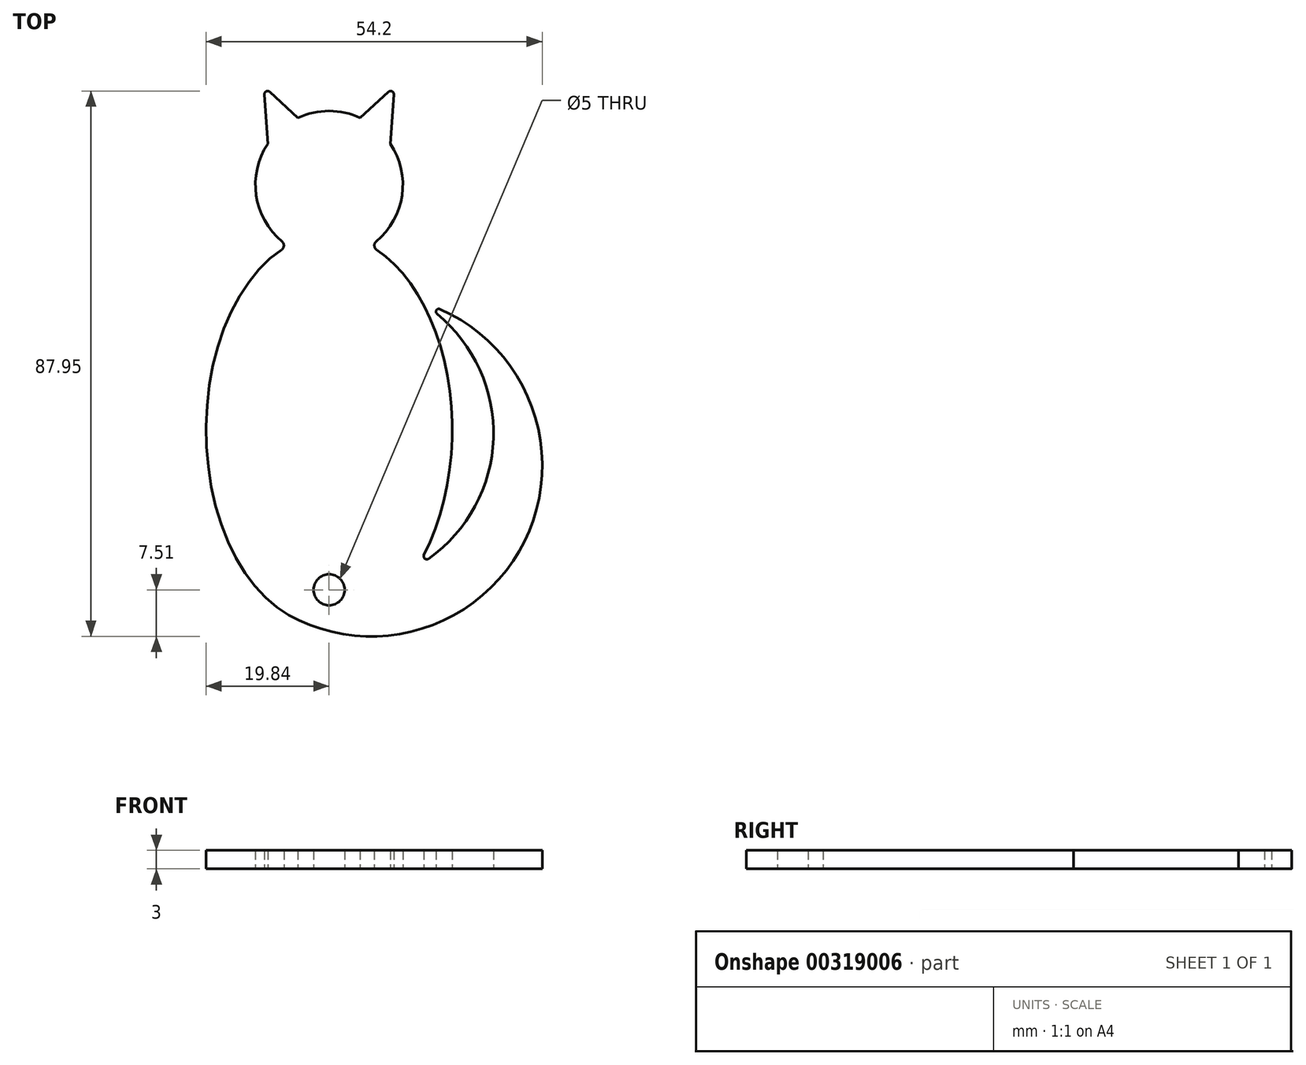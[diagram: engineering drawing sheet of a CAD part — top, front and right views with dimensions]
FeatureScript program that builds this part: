
annotation { "Feature Type Name" : "Feature", "Feature Type Description" : "" }
export const myFeature = defineFeature(function(context is Context, id is Id, definition is map)
    precondition{}
    {
        {
            var Q0;
            Q0=qCreatedBy(makeId("Top.planeOp"),FACE);
            var sketch = newSketch(context, id + "F0", { "sketchPlane" : qUnion([Q0])});
            skEllipticalArc(sketch, "E0", {});
            skArc(sketch, "E1", {"start": v(7.6, 30.45) * mm, "mid": v(11.76, 37.87) * mm, "end": v(9.9, 46.18) * mm});
            skArc(sketch, "E2.trimOffspring", {"start": v(5.02, 50.37) * mm, "mid": v(0, 51.48) * mm, "end": v(-5.02, 50.37) * mm});
            skArc(sketch, "E3", {"start": v(-6.52, -29.81) * mm, "mid": v(31.51, -17.91) * mm, "end": v(17.87, 19.53) * mm});
            skArc(sketch, "E4.trimOffspring", {"start": v(16.04, -20.73) * mm, "mid": v(26.5, -1.32) * mm, "end": v(17.4, 18.76) * mm});
            skEllipticalArc(sketch, "E5.trimOffspring", {});
            skPoint(sketch, "E6.visualSharp", {"position": v(-17.25, 15.6) * mm});
            skArc(sketch, "E6.filletArc", {"start": v(15.3, -20.09) * mm, "mid": v(15.42, -20.7) * mm, "end": v(16.04, -20.73) * mm});
            skArc(sketch, "E7", {"start": v(17.87, 19.53) * mm, "mid": v(17.3, 19.35) * mm, "end": v(17.4, 18.76) * mm});
            skPoint(sketch, "E8.visualSharp", {"position": v(6.65, 29.74) * mm});
            skArc(sketch, "E8.filletArc", {"start": v(7.6, 30.45) * mm, "mid": v(7.3, 29.76) * mm, "end": v(7.67, 29.1) * mm});
            skPoint(sketch, "E9.visualSharp", {"position": v(-6.65, 29.74) * mm});
            skArc(sketch, "E9.filletArc", {"start": v(-7.67, 29.1) * mm, "mid": v(-7.3, 29.76) * mm, "end": v(-7.6, 30.45) * mm});
            skPoint(sketch, "E10.endSnap0", {"position": v(0.2, -32.58) * mm});
            skPoint(sketch, "E11.visualSharp", {"position": v(5.14, -32.61) * mm});
            skCircle(sketch, "E12", {"center": v(0, -25.74) * mm, "radius": 2.5 * mm});
            skLineSegment(sketch, "E13", {"start": v(-9.9, 46.18) * mm, "end": v(-10.44, 54.14) * mm});
            skLineSegment(sketch, "E14", {"start": v(-9.56, 54.56) * mm, "end": v(-5.02, 50.37) * mm});
            skPoint(sketch, "E15.visualSharp", {"position": v(-10.53, 55.45) * mm});
            skArc(sketch, "E15.filletArc", {"start": v(-9.56, 54.56) * mm, "mid": v(-10.14, 54.65) * mm, "end": v(-10.44, 54.14) * mm});
            skArc(sketch, "E16.trimOffspring", {"start": v(-9.9, 46.18) * mm, "mid": v(-11.76, 37.87) * mm, "end": v(-7.6, 30.45) * mm});
            skLineSegment(sketch, "E17.MirrorCS", {"start": v(9.56, 54.56) * mm, "end": v(5.02, 50.37) * mm});
            skLineSegment(sketch, "E18.MirrorCS", {"start": v(9.9, 46.18) * mm, "end": v(10.44, 54.14) * mm});
            skArc(sketch, "E19.MirrorCS", {"start": v(9.56, 54.56) * mm, "mid": v(10.14, 54.65) * mm, "end": v(10.44, 54.14) * mm});
            const initialGuessF0  = {"E0": [0, 0, 0, 1, 0.03156074457358015, 0.019841276925391997, 0.3967115561644913, 2.8069981350632753], "E5.trimOffspring": [0, 0, 0, 1, 0.03156074457358015, 0.019841276925391997, 4.022421845958775, 5.886473751015095]};
            skSetInitialGuess(sketch, initialGuessF0);
            skSolve(sketch);
        }
        {
            var Q0;
            Q0=makeQuery(id+"F0.imprint","IMPRINT",FACE,{"disambiguationData":[TD([[makeQuery(id+"F0.imprint","IMPRINT",EDGE,{"derivedFrom":sQuery(id+"F0.wireOp",EDGE,"E0")}),1.0]])]});
            extrude(context, id + "F1", {"entities" : qUnion([Q0]), "depth" : 3 * mm});
        }
    });
